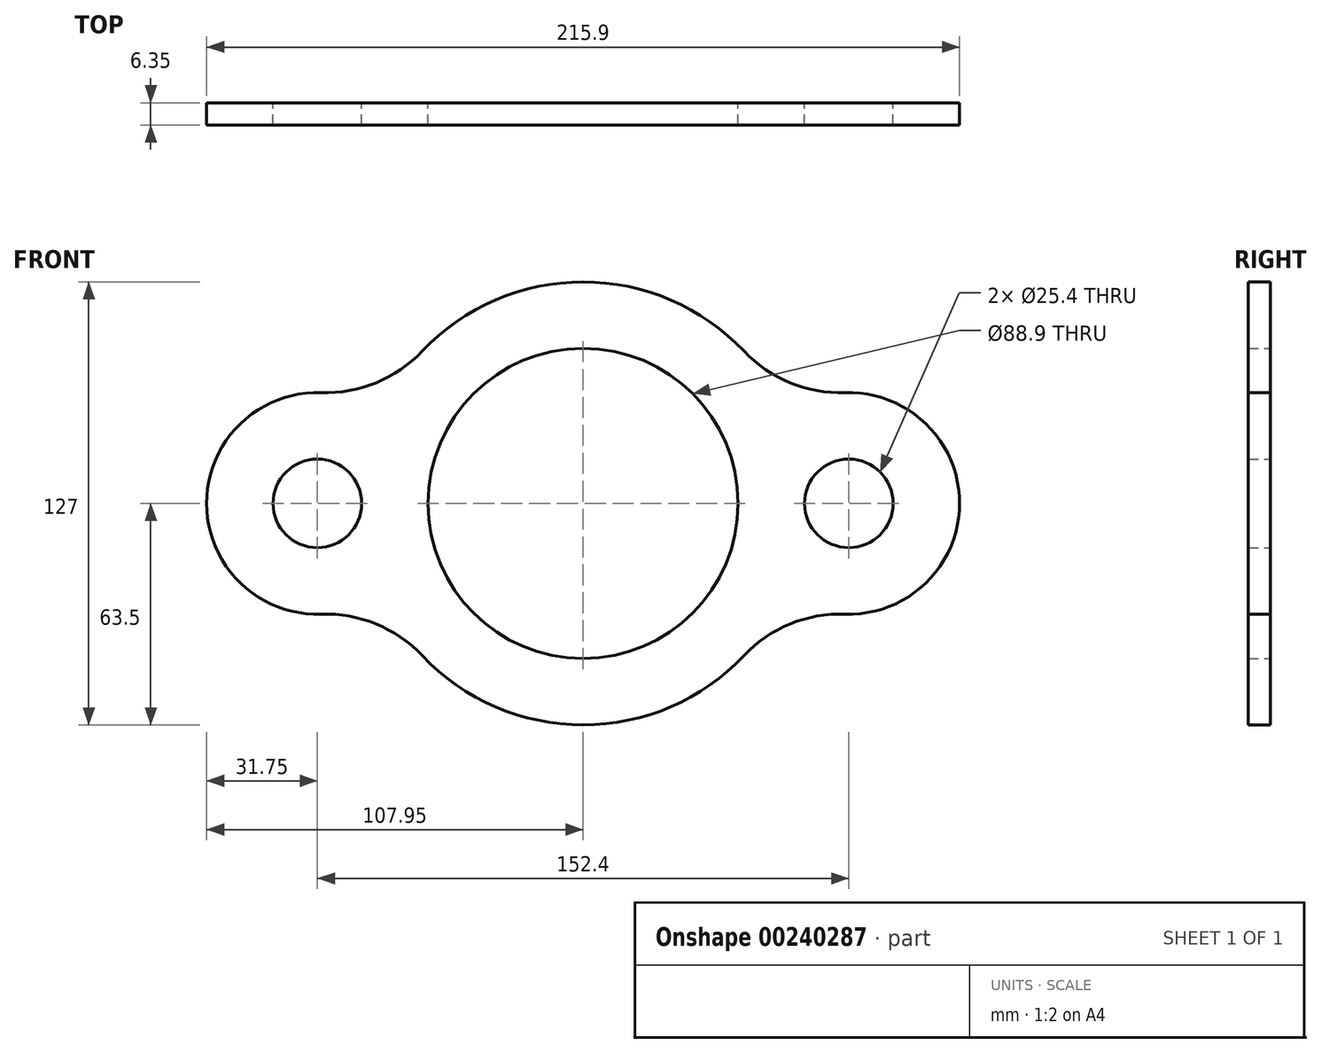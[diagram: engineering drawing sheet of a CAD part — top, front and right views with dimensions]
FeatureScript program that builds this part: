
annotation { "Feature Type Name" : "Feature", "Feature Type Description" : "" }
export const myFeature = defineFeature(function(context is Context, id is Id, definition is map)
    precondition{}
    {
        {
            var Q0;
            Q0=qCreatedBy(makeId("Front.planeOp"),FACE);
            var sketch = newSketch(context, id + "F0", { "sketchPlane" : qUnion([Q0])});
            skArc(sketch, "E0", {"start": v(46.14, 43.63) * mm, "mid": v(0, 63.5) * mm, "end": v(-46.14, 43.63) * mm});
            skCircle(sketch, "E1", {"center": v(0, 0) * mm, "radius": 44.45 * mm});
            skArc(sketch, "E2", {"start": v(75.12, -31.73) * mm, "mid": v(107.95, 0) * mm, "end": v(75.12, 31.73) * mm});
            skCircle(sketch, "E3", {"center": v(76.2, 0) * mm, "radius": 12.7 * mm});
            skArc(sketch, "E4", {"start": v(-75.12, 31.73) * mm, "mid": v(-107.95, 0) * mm, "end": v(-75.12, -31.73) * mm});
            skCircle(sketch, "E5", {"center": v(-76.2, 0) * mm, "radius": 12.7 * mm});
            skArc(sketch, "E6.trimOffspring", {"start": v(-46.14, -43.63) * mm, "mid": v(0, -63.5) * mm, "end": v(46.14, -43.63) * mm});
            skPoint(sketch, "E7.visualSharp", {"position": v(57.94, -25.98) * mm});
            skArc(sketch, "E7.filletArc", {"start": v(75.12, -31.73) * mm, "mid": v(59.35, -34.56) * mm, "end": v(46.14, -43.63) * mm});
            skPoint(sketch, "E8.visualSharp", {"position": v(57.94, 25.98) * mm});
            skArc(sketch, "E8.filletArc", {"start": v(46.14, 43.63) * mm, "mid": v(59.35, 34.56) * mm, "end": v(75.12, 31.73) * mm});
            skPoint(sketch, "E9.visualSharp", {"position": v(-57.94, 25.98) * mm});
            skArc(sketch, "E9.filletArc", {"start": v(-75.12, 31.73) * mm, "mid": v(-59.35, 34.56) * mm, "end": v(-46.14, 43.63) * mm});
            skPoint(sketch, "E10.visualSharp", {"position": v(-57.94, -25.98) * mm});
            skArc(sketch, "E10.filletArc", {"start": v(-46.14, -43.63) * mm, "mid": v(-59.35, -34.56) * mm, "end": v(-75.12, -31.73) * mm});
            skSolve(sketch);
        }
        {
            var Q0;
            Q0=makeQuery(id+"F0.imprint","IMPRINT",FACE,{"disambiguationData":[TD([[makeQuery(id+"F0.imprint","IMPRINT",EDGE,{"derivedFrom":sQuery(id+"F0.wireOp",EDGE,"E0")}),1.0]])]});
            extrude(context, id + "F1", {"entities" : qUnion([Q0]), "depth" : 6.35 * mm});
        }
    });
